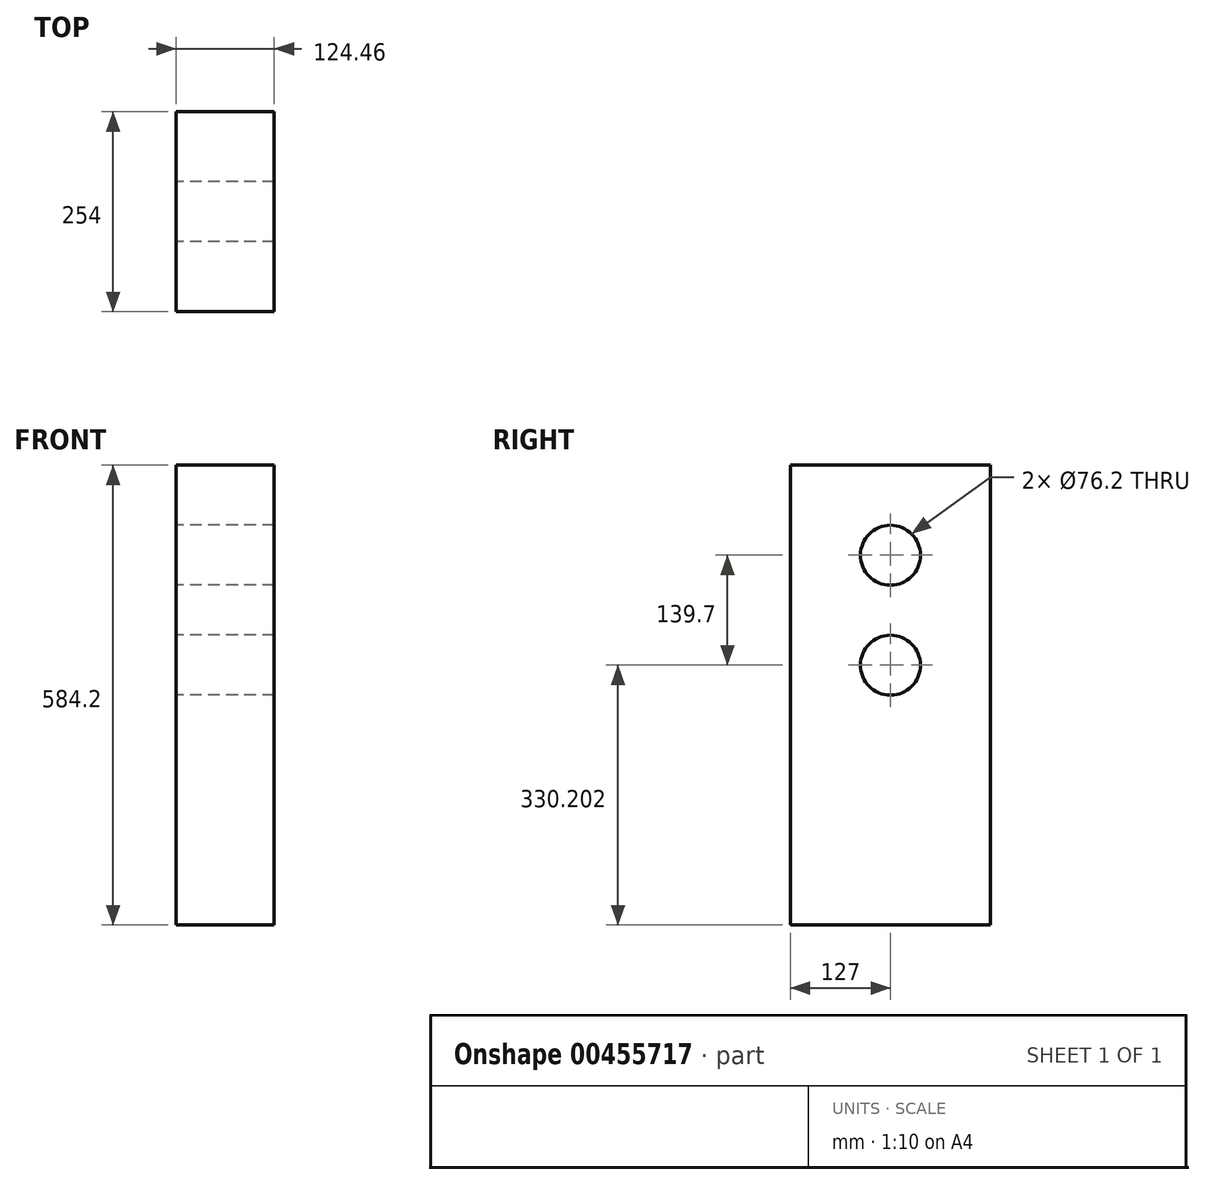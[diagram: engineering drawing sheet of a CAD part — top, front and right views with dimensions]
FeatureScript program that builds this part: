
annotation { "Feature Type Name" : "Feature", "Feature Type Description" : "" }
export const myFeature = defineFeature(function(context is Context, id is Id, definition is map)
    precondition{}
    {
        {
            var Q0;
            Q0=qCreatedBy(makeId("Front.planeOp"),FACE);
            var sketch = newSketch(context, id + "F0", { "sketchPlane" : qUnion([Q0])});
            skLineSegment(sketch, "E0.bottom", {"start": v(-62.23, -298.47) * mm, "end": v(62.23, -298.47) * mm});
            skLineSegment(sketch, "E0.top", {"start": v(-62.23, 285.73) * mm, "end": v(62.23, 285.73) * mm});
            skLineSegment(sketch, "E0.left", {"start": v(-62.23, -298.47) * mm, "end": v(-62.23, 285.73) * mm});
            skLineSegment(sketch, "E0.right", {"start": v(62.23, -298.47) * mm, "end": v(62.23, 285.73) * mm});
            skPoint(sketch, "E0.middle", {"position": v(0, -6.37) * mm});
            skSolve(sketch);
        }
        {
            var Q0;
            Q0 = qSketchRegion(id + "F0", true);
            extrude(context, id + "F1", {"entities" : qUnion([Q0]), "depth" : 254 * mm});
        }
        {
            var Q0;
            Q0=makeQuery(id+"F1.opExtrude","SWEPT_FACE",FACE,{"disambiguationData":[OSD([sQuery(id+"F0.wireOp",EDGE,"E0.left")])]});
            var sketch = newSketch(context, id + "F2", { "sketchPlane" : qUnion([Q0])});
            skCircle(sketch, "E1", {"center": v(127, 171.43) * mm, "radius": 38.1 * mm});
            skCircle(sketch, "E2", {"center": v(127, 31.73) * mm, "radius": 38.1 * mm});
            skSolve(sketch);
        }
        {
            var Q0;
            Q0 = qSketchRegion(id + "F2", true);
            extrude(context, id + "F3", {"entities" : qUnion([Q0]), "operationType" : NewBodyOperationType.REMOVE, "oppositeDirection" : true, "depth" : 185.42 * mm});
        }
    });
